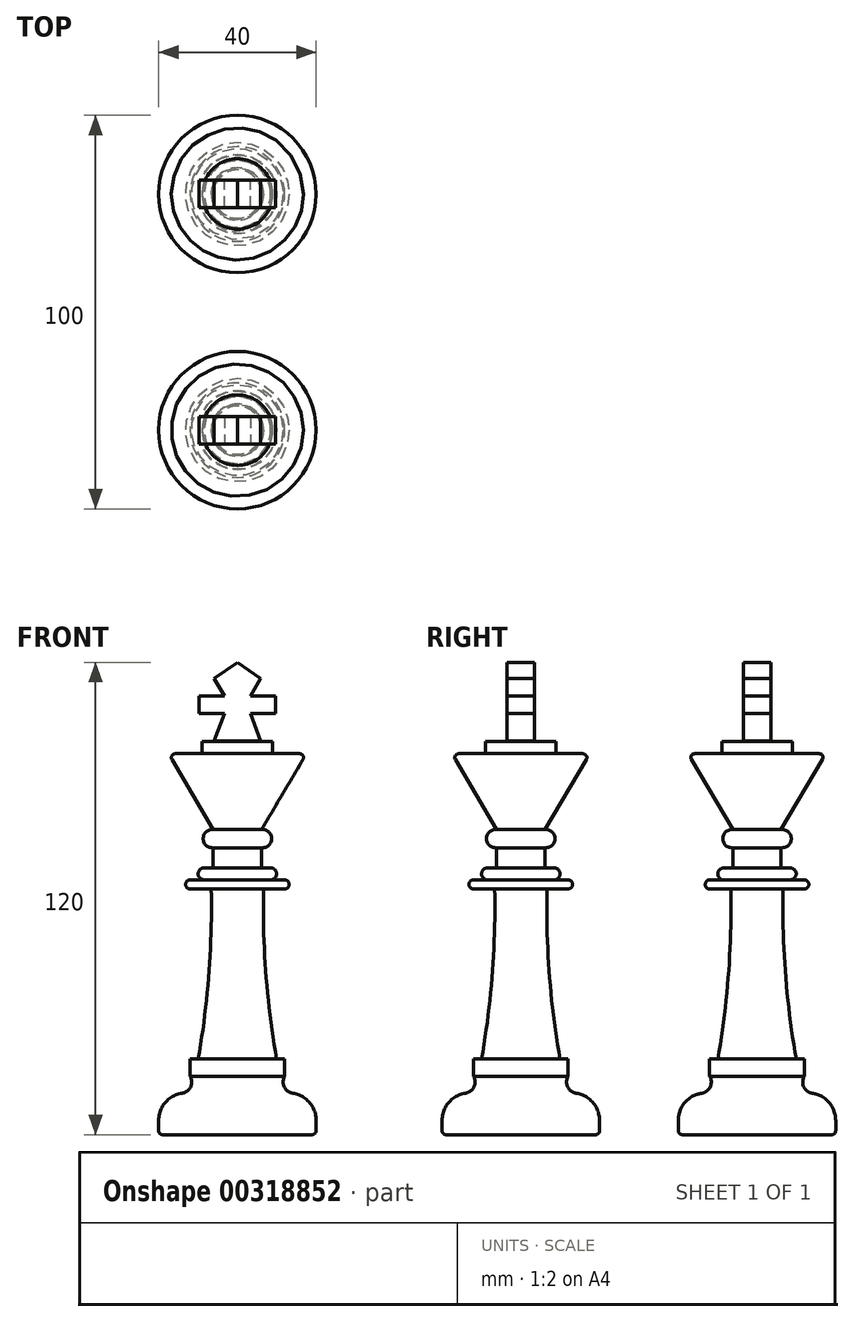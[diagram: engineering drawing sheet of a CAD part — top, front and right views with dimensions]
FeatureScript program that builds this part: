
annotation { "Feature Type Name" : "Feature", "Feature Type Description" : "" }
export const myFeature = defineFeature(function(context is Context, id is Id, definition is map)
    precondition{}
    {
        {
            var Q0;
            Q0=qCreatedBy(makeId("Front.planeOp"),FACE);
            var sketch = newSketch(context, id + "F0", { "sketchPlane" : qUnion([Q0])});
            skLineSegment(sketch, "E0", {"start": v(0, 40) * mm, "end": v(0, -60) * mm});
            skLineSegment(sketch, "E1", {"start": v(0, -60) * mm, "end": v(-20, -60) * mm});
            skLineSegment(sketch, "E2", {"start": v(-20, -60) * mm, "end": v(-20, -56.38) * mm});
            skArc(sketch, "E3", {"start": v(-14.06, -49.47) * mm, "mid": v(-18.31, -51.83) * mm, "end": v(-20, -56.38) * mm});
            skArc(sketch, "E4", {"start": v(-14.06, -49.47) * mm, "mid": v(-11.89, -47.84) * mm, "end": v(-12.02, -45.13) * mm});
            skLineSegment(sketch, "E5", {"start": v(-12.02, -45.13) * mm, "end": v(-12.02, -40.78) * mm});
            skLineSegment(sketch, "E6", {"start": v(-12.02, -40.78) * mm, "end": v(-9.97, -40.78) * mm});
            skArc(sketch, "E7", {"start": v(-9.97, -40.78) * mm, "mid": v(-7.25, -19.26) * mm, "end": v(-6.65, 2.43) * mm});
            skLineSegment(sketch, "E8", {"start": v(-6.65, 2.43) * mm, "end": v(-12.02, 2.43) * mm});
            skArc(sketch, "E9", {"start": v(-12.02, 4.73) * mm, "mid": v(-13.17, 3.58) * mm, "end": v(-12.02, 2.43) * mm});
            skLineSegment(sketch, "E10", {"start": v(-12.02, 4.73) * mm, "end": v(-8.44, 4.73) * mm});
            skArc(sketch, "E11", {"start": v(-8.44, 7.8) * mm, "mid": v(-9.97, 6.26) * mm, "end": v(-8.44, 4.73) * mm});
            skLineSegment(sketch, "E12", {"start": v(-8.44, 7.8) * mm, "end": v(-6.14, 7.8) * mm});
            skLineSegment(sketch, "E13", {"start": v(-6.14, 7.8) * mm, "end": v(-6.14, 12.91) * mm});
            skArc(sketch, "E14", {"start": v(-6.14, 17.51) * mm, "mid": v(-8.7, 15.21) * mm, "end": v(-6.14, 12.91) * mm});
            skLineSegment(sketch, "E15", {"start": v(-6.14, 17.51) * mm, "end": v(-17.54, 36.8) * mm});
            skLineSegment(sketch, "E16", {"start": v(-8.95, 36.8) * mm, "end": v(-17.54, 36.8) * mm});
            skLineSegment(sketch, "E17", {"start": v(-8.95, 36.8) * mm, "end": v(-8.95, 39.87) * mm});
            skLineSegment(sketch, "E18", {"start": v(-8.95, 39.87) * mm, "end": v(0, 40) * mm});
            skLineSegment(sketch, "E19", {"start": v(0, 65.84) * mm, "end": v(0, -87.57) * mm, "construction": true});
            skSolve(sketch);
        }
        {
            var Q0;
            Q0=makeQuery(id+"F0.imprint","IMPRINT",FACE,{"disambiguationData":[TD([[makeQuery(id+"F0.imprint","IMPRINT",EDGE,{"derivedFrom":sQuery(id+"F0.wireOp",EDGE,"E0")}),-1.0]])]});
            var Q1;
            Q1=sQuery(id+"F0.wireOp",EDGE,"E19");
            revolve(context, id + "F1", {"entities" : qUnion([Q0]), "axis" : qUnion([Q1]), "revolveType" : RevolveType.FULL});
        }
        {
            var Q0;
            Q0=qCreatedBy(makeId("Front.planeOp"),FACE);
            var sketch = newSketch(context, id + "F2", { "sketchPlane" : qUnion([Q0])});
            skLineSegment(sketch, "E20", {"start": v(0, 0) * mm, "end": v(0, 60) * mm, "construction": true});
            skLineSegment(sketch, "E21", {"start": v(0, 40) * mm, "end": v(-5.88, 40) * mm});
            skLineSegment(sketch, "E22", {"start": v(-5.88, 40) * mm, "end": v(-3.32, 46.97) * mm});
            skLineSegment(sketch, "E23", {"start": v(-3.32, 46.97) * mm, "end": v(-9.7, 46.97) * mm});
            skLineSegment(sketch, "E24", {"start": v(-9.7, 46.97) * mm, "end": v(-9.7, 51.43) * mm});
            skLineSegment(sketch, "E25", {"start": v(-9.7, 51.43) * mm, "end": v(-3.32, 51.43) * mm});
            skLineSegment(sketch, "E26", {"start": v(-3.32, 51.43) * mm, "end": v(-5.88, 55.85) * mm});
            skLineSegment(sketch, "E27", {"start": v(-5.88, 55.85) * mm, "end": v(0, 60) * mm});
            skLineSegment(sketch, "E28.MirrorCS", {"start": v(5.88, 55.85) * mm, "end": v(0, 60) * mm});
            skLineSegment(sketch, "E29.MirrorCS", {"start": v(3.32, 51.43) * mm, "end": v(5.88, 55.85) * mm});
            skLineSegment(sketch, "E30.MirrorCS", {"start": v(9.7, 51.43) * mm, "end": v(3.32, 51.43) * mm});
            skLineSegment(sketch, "E31.MirrorCS", {"start": v(9.7, 46.97) * mm, "end": v(9.7, 51.43) * mm});
            skLineSegment(sketch, "E32.MirrorCS", {"start": v(3.32, 46.97) * mm, "end": v(9.7, 46.97) * mm});
            skLineSegment(sketch, "E33.MirrorCS", {"start": v(5.88, 40) * mm, "end": v(3.32, 46.97) * mm});
            skLineSegment(sketch, "E34.MirrorCS", {"start": v(0, 40) * mm, "end": v(5.88, 40) * mm});
            skSolve(sketch);
        }
        {
            var Q0;
            Q0=makeQuery(id+"F2.imprint","IMPRINT",FACE,{"disambiguationData":[TD([[makeQuery(id+"F2.imprint","IMPRINT",EDGE,{"derivedFrom":sQuery(id+"F2.wireOp",EDGE,"E22")}),-1.0]])]});
            extrude(context, id + "F3", {"entities" : qUnion([Q0]), "operationType" : NewBodyOperationType.ADD, "endBound" : BoundingType.SYMMETRIC, "depth" : 7 * mm});
        }
        {
            var Q0;
            Q0=makeQuery(id+"F1.opRevolve","SWEPT_EDGE",EDGE,{"disambiguationData":[OSD([sQuery(id+"F0.wireOp",EDGE,"E15"),sQuery(id+"F0.wireOp",EDGE,"E16")])]});
            var Q1;
            Q1=makeQuery(id+"F1.opRevolve","SWEPT_EDGE",EDGE,{"disambiguationData":[OSD([sQuery(id+"F0.wireOp",EDGE,"E1"),sQuery(id+"F0.wireOp",EDGE,"E2")])]});
            fillet(context, id + "F4", {"entities" : qUnion([Q0, Q1]), "radius" : 1 * mm, "tangentPropagation" : true, "allowEdgeOverflow" : false});
        }
        {
            var Q0;
            Q0=qCreatedBy(makeId("Front.planeOp"),FACE);
            cPlane(context, id + "F5", {"entities" : qUnion([Q0]), "cplaneType" : CPlaneType.OFFSET, "offset" : 30 * mm, "width" : 150 * mm, "height" : 150 * mm});
        }
        {
            var Q0;
            Q0=makeQuery(id+"F3.opExtrude","SWEPT_BODY",BODY,{"disambiguationData":[OSD([sQuery(id+"F2.wireOp",EDGE,"E22"),sQuery(id+"F2.wireOp",EDGE,"E23"),sQuery(id+"F2.wireOp",EDGE,"E24"),sQuery(id+"F2.wireOp",EDGE,"E25"),sQuery(id+"F2.wireOp",EDGE,"E26"),sQuery(id+"F2.wireOp",EDGE,"E27"),sQuery(id+"F2.wireOp",EDGE,"E28.MirrorCS"),sQuery(id+"F2.wireOp",EDGE,"E29.MirrorCS"),sQuery(id+"F2.wireOp",EDGE,"E30.MirrorCS"),sQuery(id+"F2.wireOp",EDGE,"E31.MirrorCS"),sQuery(id+"F2.wireOp",EDGE,"E32.MirrorCS"),sQuery(id+"F2.wireOp",EDGE,"E33.MirrorCS"),sQuery(id+"F2.wireOp",EDGE,"E34.MirrorCS"),sQuery(id+"F2.wireOp",EDGE,"E21")])]});
            var Q1;
            Q1=makeQuery(id+"F1.opRevolve","SWEPT_BODY",BODY,{"disambiguationData":[OSD([sQuery(id+"F0.wireOp",EDGE,"E0"),sQuery(id+"F0.wireOp",EDGE,"E1"),sQuery(id+"F0.wireOp",EDGE,"E2"),sQuery(id+"F0.wireOp",EDGE,"E3"),sQuery(id+"F0.wireOp",EDGE,"E4"),sQuery(id+"F0.wireOp",EDGE,"E5"),sQuery(id+"F0.wireOp",EDGE,"E6"),sQuery(id+"F0.wireOp",EDGE,"E7"),sQuery(id+"F0.wireOp",EDGE,"E8"),sQuery(id+"F0.wireOp",EDGE,"E9"),sQuery(id+"F0.wireOp",EDGE,"E10"),sQuery(id+"F0.wireOp",EDGE,"E11"),sQuery(id+"F0.wireOp",EDGE,"E12"),sQuery(id+"F0.wireOp",EDGE,"E13"),sQuery(id+"F0.wireOp",EDGE,"E14"),sQuery(id+"F0.wireOp",EDGE,"E15"),sQuery(id+"F0.wireOp",EDGE,"E16"),sQuery(id+"F0.wireOp",EDGE,"E17"),sQuery(id+"F0.wireOp",EDGE,"E18")])]});
            var Q2;
            Q2=qCreatedBy(id+"F5.planeOp",FACE);
            mirror(context, id + "F6", {"entities" : qUnion([Q0, Q1]), "mirrorPlane" : qUnion([Q2])});
        }
    });
